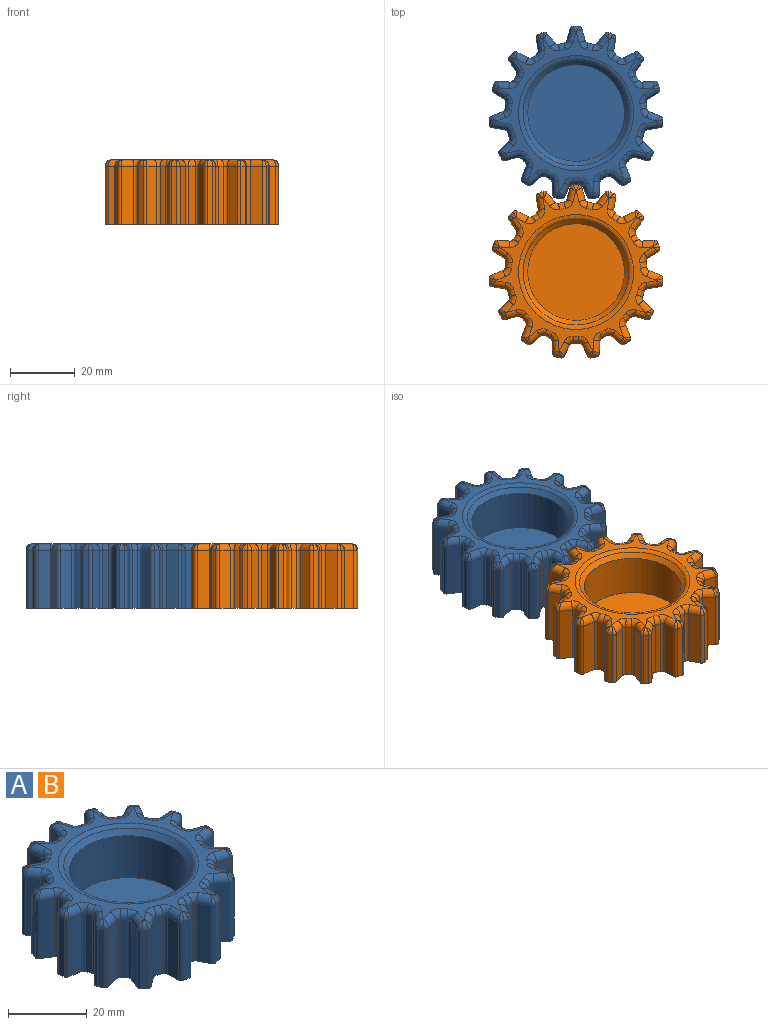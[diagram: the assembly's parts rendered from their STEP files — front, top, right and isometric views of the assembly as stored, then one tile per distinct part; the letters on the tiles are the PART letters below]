
ASSEMBLY  parts=2 mates=1
PART A: 246 faces, bbox 54x53.7x20 mm
  f0: cylinder r=1mm len=18mm, axis (0,0,-1), area 20.6mm2, adj f1,f119,f121,f242
  f1: cylinder r=22mm len=18mm, axis (0,0,-1), area 34.5mm2, adj f0,f2,f121,f240
  f2: cylinder r=1mm len=18mm, axis (0,0,-1), area 20.6mm2, adj f1,f3,f121,f238
  f3: plane 18x3.33mm, normal (0.84,-0.54,0), area 71.4mm2, adj f2,f4,f121,f236
  f4: cylinder r=1mm len=18mm, axis (0,0,-1), area 23.6mm2, adj f3,f5,f121,f234
  f5: plane 18x1.25mm, normal (0.74,0.67,0), area 30.2mm2, adj f4,f6,f121,f232
  f6: cylinder r=1mm len=18mm, axis (0,0,-1), area 23.6mm2, adj f5,f7,f121,f230
  f7: plane 18x3.54mm, normal (-0.45,0.89,0), area 71.4mm2, adj f6,f8,f121,f228
  f8: cylinder r=1mm len=18mm, axis (0,0,-1), area 20.6mm2, adj f7,f9,f121,f226
  f9: cylinder r=22mm len=18mm, axis (0,0,-1), area 34.5mm2, adj f8,f10,f121,f224
  f10: cylinder r=1mm len=18mm, axis (0,0,-1), area 20.6mm2, adj f9,f11,f121,f222
  f11: plane 18x3.92mm, normal (0.99,-0.16,0), area 71.4mm2, adj f10,f12,f121,f220
  f12: cylinder r=1mm len=18mm, axis (0,0,-1), area 23.6mm2, adj f11,f13,f121,f218
  f13: plane 18x1.53mm, normal (0.41,0.91,0), area 30.2mm2, adj f12,f14,f121,f216
  f14: cylinder r=1mm len=18mm, axis (0,0,-1), area 23.6mm2, adj f13,f15,f121,f214
  f15: plane 18x3.08mm, normal (-0.78,0.63,0), area 71.4mm2, adj f14,f16,f121,f212
  f16: cylinder r=1mm len=18mm, axis (0,0,-1), area 20.6mm2, adj f15,f17,f121,f210
  f17: cylinder r=22mm len=18mm, axis (0,0,-1), area 34.5mm2, adj f16,f18,f121,f208
  f18: cylinder r=1mm len=18mm, axis (0,0,-1), area 20.6mm2, adj f17,f19,f121,f206
  f19: plane 18x3.83mm, normal (0.97,0.26,0), area 71.4mm2, adj f18,f20,f121,f204
  f20: cylinder r=1mm len=18mm, axis (0,0,-1), area 23.6mm2, adj f19,f21,f121,f202
  f21: plane 18x1.68mm, normal (0,1,0), area 30.2mm2, adj f20,f22,f121,f200
  f22: cylinder r=1mm len=18mm, axis (0,0,-1), area 23.6mm2, adj f21,f23,f121,f198
  f23: plane 18x3.83mm, normal (-0.97,0.26,0), area 71.4mm2, adj f22,f24,f121,f196
  f24: cylinder r=1mm len=18mm, axis (0,0,-1), area 20.6mm2, adj f23,f25,f121,f194
  f25: cylinder r=22mm len=18mm, axis (0,0,-1), area 34.5mm2, adj f24,f26,f121,f192
  f26: cylinder r=1mm len=18mm, axis (0,0,-1), area 20.6mm2, adj f25,f27,f121,f190
  f27: plane 18x3.08mm, normal (0.78,0.63,0), area 71.4mm2, adj f26,f28,f121,f188
  f28: cylinder r=1mm len=18mm, axis (0,0,-1), area 23.6mm2, adj f27,f29,f121,f186
  f29: plane 18x1.53mm, normal (-0.41,0.91,0), area 30.2mm2, adj f28,f30,f121,f184
  f30: cylinder r=1mm len=18mm, axis (0,0,-1), area 23.6mm2, adj f29,f31,f121,f182
  f31: plane 18x3.92mm, normal (-0.99,-0.16,0), area 71.4mm2, adj f30,f32,f121,f180
  f32: cylinder r=1mm len=18mm, axis (0,0,-1), area 20.6mm2, adj f31,f33,f121,f178
  f33: cylinder r=22mm len=18mm, axis (0,0,-1), area 34.5mm2, adj f32,f34,f121,f176
  f34: cylinder r=1mm len=18mm, axis (0,0,-1), area 20.6mm2, adj f33,f35,f121,f174
  f35: plane 18x3.54mm, normal (0.45,0.89,0), area 71.4mm2, adj f34,f36,f121,f172
  f36: cylinder r=1mm len=18mm, axis (0,0,-1), area 23.6mm2, adj f35,f37,f121,f170
  f37: plane 18x1.25mm, normal (-0.74,0.67,0), area 30.2mm2, adj f36,f38,f121,f168
  f38: cylinder r=1mm len=18mm, axis (0,0,-1), area 23.6mm2, adj f37,f39,f121,f166
  f39: plane 18x3.33mm, normal (-0.84,-0.54,0), area 71.4mm2, adj f38,f40,f121,f164
  f40: cylinder r=1mm len=18mm, axis (0,0,-1), area 20.6mm2, adj f39,f41,f121,f162
  f41: cylinder r=22mm len=18mm, axis (0,0,-1), area 34.5mm2, adj f40,f42,f121,f160
  f42: cylinder r=1mm len=18mm, axis (0,0,-1), area 20.6mm2, adj f41,f43,f121,f158
  f43: plane 18x3.96mm, normal (0.05,1,0), area 71.4mm2, adj f42,f44,f121,f156
  f44: cylinder r=1mm len=18mm, axis (0,0,-1), area 23.6mm2, adj f43,f45,f121,f154
  f45: plane 18x1.59mm, normal (-0.95,0.31,0), area 30.2mm2, adj f44,f46,f121,f152
  f46: cylinder r=1mm len=18mm, axis (0,0,-1), area 23.6mm2, adj f45,f47,f121,f150
  f47: plane 18x3.33mm, normal (-0.54,-0.84,0), area 71.4mm2, adj f46,f48,f121,f148
  f48: cylinder r=1mm len=18mm, axis (0,0,-1), area 20.6mm2, adj f47,f49,f121,f146
  f49: cylinder r=22mm len=18mm, axis (0,0,-1), area 34.5mm2, adj f48,f50,f121,f144
  f50: cylinder r=1mm len=18mm, axis (0,0,-1), area 20.6mm2, adj f49,f51,f121,f142
  f51: plane 18x3.71mm, normal (-0.36,0.93,0), area 71.4mm2, adj f50,f52,f121,f140
  f52: cylinder r=1mm len=18mm, axis (0,0,-1), area 23.6mm2, adj f51,f53,f121,f138
  f53: plane 18x1.67mm, normal (-0.99,-0.1,0), area 30.2mm2, adj f52,f54,f121,f136
  f54: cylinder r=1mm len=18mm, axis (0,0,-1), area 23.6mm2, adj f53,f55,f121,f134
  f55: plane 18x3.92mm, normal (-0.16,-0.99,0), area 71.4mm2, adj f54,f56,f121,f132
  f56: cylinder r=1mm len=18mm, axis (0,0,-1), area 20.6mm2, adj f55,f57,f121,f130
  f57: cylinder r=22mm len=18mm, axis (0,0,-1), area 34.5mm2, adj f56,f58,f121,f128
  f58: cylinder r=1mm len=18mm, axis (0,0,-1), area 20.6mm2, adj f57,f59,f121,f126
  f59: plane 18x2.81mm, normal (-0.71,0.71,0), area 71.4mm2, adj f58,f60,f121,f127
  f60: cylinder r=1mm len=18mm, axis (0,0,-1), area 23.6mm2, adj f59,f61,f121,f129
  f61: plane 18x1.45mm, normal (-0.87,-0.5,0), area 30.2mm2, adj f60,f62,f121,f131
  f62: cylinder r=1mm len=18mm, axis (0,0,-1), area 23.6mm2, adj f61,f63,f121,f133
  f63: plane 18x3.83mm, normal (0.26,-0.97,0), area 71.4mm2, adj f62,f64,f121,f135
  f64: cylinder r=1mm len=18mm, axis (0,0,-1), area 20.6mm2, adj f63,f65,f121,f137
  f65: cylinder r=22mm len=18mm, axis (0,0,-1), area 34.5mm2, adj f64,f66,f121,f139
  f66: cylinder r=1mm len=18mm, axis (0,0,-1), area 20.6mm2, adj f65,f67,f121,f141
  f67: plane 18x3.71mm, normal (-0.93,0.36,0), area 71.4mm2, adj f66,f68,f121,f143
  f68: cylinder r=1mm len=18mm, axis (0,0,-1), area 23.6mm2, adj f67,f69,f121,f145
  f69: plane 18x1.36mm, normal (-0.59,-0.81,0), area 30.2mm2, adj f68,f70,f121,f147
  f70: cylinder r=1mm len=18mm, axis (0,0,-1), area 23.6mm2, adj f69,f71,f121,f149
  f71: plane 18x3.08mm, normal (0.63,-0.78,0), area 71.4mm2, adj f70,f72,f121,f151
  f72: cylinder r=1mm len=18mm, axis (0,0,-1), area 20.6mm2, adj f71,f73,f121,f153
  f73: cylinder r=22mm len=18mm, axis (0,0,-1), area 34.5mm2, adj f72,f74,f121,f155
  f74: cylinder r=1mm len=18mm, axis (0,0,-1), area 20.6mm2, adj f73,f75,f121,f157
  f75: plane 18x3.96mm, normal (-1,-0.05,0), area 71.4mm2, adj f74,f76,f121,f159
  f76: cylinder r=1mm len=18mm, axis (0,0,-1), area 23.6mm2, adj f75,f77,f121,f161
  f77: plane 18x1.64mm, normal (-0.21,-0.98,0), area 30.2mm2, adj f76,f78,f121,f163
  f78: cylinder r=1mm len=18mm, axis (0,0,-1), area 23.6mm2, adj f77,f79,f121,f165
  f79: plane 18x3.54mm, normal (0.89,-0.45,0), area 71.4mm2, adj f78,f80,f121,f167
  f80: cylinder r=1mm len=18mm, axis (0,0,-1), area 20.6mm2, adj f79,f81,f121,f169
  f81: cylinder r=22mm len=18mm, axis (0,0,-1), area 34.5mm2, adj f80,f82,f121,f171
  f82: cylinder r=1mm len=18mm, axis (0,0,-1), area 20.6mm2, adj f81,f83,f121,f173
  f83: plane 18x3.54mm, normal (-0.89,-0.45,0), area 71.4mm2, adj f82,f84,f121,f175
  f84: cylinder r=1mm len=18mm, axis (0,0,-1), area 23.6mm2, adj f83,f85,f121,f177
  f85: plane 18x1.64mm, normal (0.21,-0.98,0), area 30.2mm2, adj f84,f86,f121,f179
  f86: cylinder r=1mm len=18mm, axis (0,0,-1), area 23.6mm2, adj f85,f87,f121,f181
  f87: plane 18x3.96mm, normal (1,-0.05,0), area 71.4mm2, adj f86,f88,f121,f183
  f88: cylinder r=1mm len=18mm, axis (0,0,-1), area 20.6mm2, adj f87,f89,f121,f185
  f89: cylinder r=22mm len=18mm, axis (0,0,-1), area 34.5mm2, adj f88,f90,f121,f187
  f90: cylinder r=1mm len=18mm, axis (0,0,-1), area 20.6mm2, adj f89,f91,f121,f189
  f91: plane 18x3.08mm, normal (-0.63,-0.78,0), area 71.4mm2, adj f90,f92,f121,f191
  f92: cylinder r=1mm len=18mm, axis (0,0,-1), area 23.6mm2, adj f91,f93,f121,f193
  f93: plane 18x1.36mm, normal (0.59,-0.81,0), area 30.2mm2, adj f92,f94,f121,f195
  f94: cylinder r=1mm len=18mm, axis (0,0,-1), area 23.6mm2, adj f93,f95,f121,f197
  f95: plane 18x3.71mm, normal (0.93,0.36,0), area 71.4mm2, adj f94,f96,f121,f199
  f96: cylinder r=1mm len=18mm, axis (0,0,-1), area 20.6mm2, adj f95,f97,f121,f201
  f97: cylinder r=22mm len=18mm, axis (0,0,-1), area 34.5mm2, adj f96,f98,f121,f203
  f98: cylinder r=1mm len=18mm, axis (0,0,-1), area 20.6mm2, adj f97,f99,f121,f205
  f99: plane 18x3.83mm, normal (-0.26,-0.97,0), area 71.4mm2, adj f98,f100,f121,f207
  f100: cylinder r=1mm len=18mm, axis (0,0,-1), area 23.6mm2, adj f99,f101,f121,f209
  f101: plane 18x1.45mm, normal (0.87,-0.5,0), area 30.2mm2, adj f100,f102,f121,f211
  f102: cylinder r=1mm len=18mm, axis (0,0,-1), area 23.6mm2, adj f101,f103,f121,f213
  f103: plane 18x2.81mm, normal (0.71,0.71,0), area 71.4mm2, adj f102,f104,f121,f215
  f104: cylinder r=1mm len=18mm, axis (0,0,-1), area 20.6mm2, adj f103,f105,f121,f217
  f105: cylinder r=22mm len=18mm, axis (0,0,-1), area 34.5mm2, adj f104,f106,f121,f219
  f106: cylinder r=1mm len=18mm, axis (0,0,-1), area 20.6mm2, adj f105,f107,f121,f221
  f107: plane 18x3.92mm, normal (0.16,-0.99,0), area 71.4mm2, adj f106,f108,f121,f223
  f108: cylinder r=1mm len=18mm, axis (0,0,-1), area 23.6mm2, adj f107,f109,f121,f225
  f109: plane 18x1.67mm, normal (0.99,-0.1,0), area 30.2mm2, adj f108,f110,f121,f227
  f110: cylinder r=1mm len=18mm, axis (0,0,-1), area 23.6mm2, adj f109,f111,f121,f229
  f111: plane 18x3.71mm, normal (0.36,0.93,0), area 71.4mm2, adj f110,f112,f121,f231
  f112: cylinder r=1mm len=18mm, axis (0,0,-1), area 20.6mm2, adj f111,f113,f121,f233
  f113: cylinder r=22mm len=18mm, axis (0,0,-1), area 34.5mm2, adj f112,f114,f121,f235
  f114: cylinder r=1mm len=18mm, axis (0,0,-1), area 20.6mm2, adj f113,f115,f121,f237
  f115: plane 18x3.33mm, normal (0.54,-0.84,0), area 71.4mm2, adj f114,f116,f121,f239
  f116: cylinder r=1mm len=18mm, axis (0,0,-1), area 23.6mm2, adj f115,f117,f121,f241
  f117: plane 18x1.59mm, normal (0.95,0.31,0), area 30.2mm2, adj f116,f118,f121,f243
  f118: cylinder r=1mm len=18mm, axis (0,0,-1), area 23.6mm2, adj f117,f119,f121,f245
  f119: plane 18x3.96mm, normal (-0.05,1,0), area 71.4mm2, adj f0,f118,f121,f244
  f120: plane 49.74x49.47mm, normal (0,0,1), area 390.9mm2, adj f125,f126,f127,f128,f130,f131,f132,f135
  f121: plane 53.89x53.61mm, normal (0,0,-1), area 1866.6mm2, adj f0,f1,f2,f3,f4,f5,f6,f7
  f122: cylinder r=15mm len=30mm, axis (0,0,1), area 1225.2mm2, adj f123,f124
  f123: plane 30x30mm, normal (0,0,1), area 706.9mm2, adj f122
  f124: cone r=15mm half-angle=45deg, axis (0,0,1), area 197.4mm2, adj f122,f125
  f125: torus R=17.83mm, axis (0,0,1), area 168.6mm2, adj f120,f124
  f126: torus R=3mm, axis (0,0,1), area 6.2mm2, adj f58,f120,f127,f128
  f127: cylinder r=2mm len=4.22mm, axis (0.71,0.71,0), area 11.6mm2, adj f59,f120,f126,f129
  f128: torus R=20mm, axis (0,0,1), area 5.8mm2, adj f57,f120,f126,f130
  f129: bspline ~2.5x2.34mm, area 2.7mm2, adj f60,f127,f131
  f130: torus R=3mm, axis (0,0,1), area 6.2mm2, adj f56,f120,f128,f132
  f131: cylinder r=2mm len=2.57mm, axis (-0.5,0.87,0), area 3.5mm2, adj f61,f120,f129,f133
  f132: cylinder r=2mm len=4.23mm, axis (-0.99,0.16,0), area 11.6mm2, adj f55,f120,f130,f134
  f133: bspline ~2.34x2.33mm, area 2.7mm2, adj f62,f131,f135
  f134: bspline ~2.34x1.91mm, area 2.7mm2, adj f54,f132,f136
  f135: cylinder r=2mm len=4.35mm, axis (-0.97,-0.26,0), area 11.6mm2, adj f63,f120,f133,f137
  f136: cylinder r=2mm len=2.16mm, axis (-0.1,0.99,0), area 3.5mm2, adj f53,f120,f134,f138
  f137: torus R=3mm, axis (0,0,1), area 6.2mm2, adj f64,f120,f135,f139
  f138: bspline ~2.34x2.15mm, area 2.7mm2, adj f52,f136,f140
  f139: torus R=20mm, axis (0,0,1), area 5.8mm2, adj f65,f120,f137,f141
  f140: cylinder r=2mm len=4.42mm, axis (0.93,0.36,0), area 11.6mm2, adj f51,f120,f138,f142
  f141: torus R=3mm, axis (0,0,1), area 6.2mm2, adj f66,f120,f139,f143
  f142: torus R=3mm, axis (0,0,1), area 6.2mm2, adj f50,f120,f140,f144
  f143: cylinder r=2mm len=4.42mm, axis (0.36,0.93,0), area 11.6mm2, adj f67,f120,f141,f145
  f144: torus R=20mm, axis (0,0,1), area 5.8mm2, adj f49,f120,f142,f146
  f145: bspline ~2.42x2.34mm, area 2.7mm2, adj f68,f143,f147
  f146: torus R=3mm, axis (0,0,1), area 6.2mm2, adj f48,f120,f144,f148
  f147: cylinder r=2mm len=2.6mm, axis (-0.81,0.59,0), area 3.5mm2, adj f69,f120,f145,f149
  f148: cylinder r=2mm len=4.42mm, axis (-0.84,0.54,0), area 11.6mm2, adj f47,f120,f146,f150
  f149: bspline ~2.52x2.34mm, area 2.7mm2, adj f70,f147,f151
  f150: bspline ~2.38x2.34mm, area 2.7mm2, adj f46,f148,f152
  f151: cylinder r=2mm len=4.34mm, axis (-0.78,-0.63,0), area 11.6mm2, adj f71,f120,f149,f153
  f152: cylinder r=2mm len=2.42mm, axis (0.31,0.95,0), area 3.5mm2, adj f45,f120,f150,f154
  f153: torus R=3mm, axis (0,0,1), area 6.2mm2, adj f72,f120,f151,f155
  f154: bspline ~2.34x2.08mm, area 2.7mm2, adj f44,f152,f156
  f155: torus R=20mm, axis (0,0,1), area 5.8mm2, adj f73,f120,f153,f157
  f156: cylinder r=2mm len=4.07mm, axis (1,-0.05,0), area 11.6mm2, adj f43,f120,f154,f158
  f157: torus R=3mm, axis (0,0,1), area 6.2mm2, adj f74,f120,f155,f159
  f158: torus R=3mm, axis (0,0,1), area 6.2mm2, adj f42,f120,f156,f160
  f159: cylinder r=2mm len=4.07mm, axis (-0.05,1,0), area 11.6mm2, adj f75,f120,f157,f161
  f160: torus R=20mm, axis (0,0,1), area 5.8mm2, adj f41,f120,f158,f162
  f161: bspline ~2.34x1.96mm, area 2.7mm2, adj f76,f159,f163
  f162: torus R=3mm, axis (0,0,1), area 6.2mm2, adj f40,f120,f160,f164
  f163: cylinder r=2mm len=2.3mm, axis (-0.98,0.21,0), area 3.5mm2, adj f77,f120,f161,f165
  f164: cylinder r=2mm len=4.42mm, axis (-0.54,0.84,0), area 11.6mm2, adj f39,f120,f162,f166
  f165: bspline ~2.34x2.28mm, area 2.7mm2, adj f78,f163,f167
  f166: bspline ~2.51x2.34mm, area 2.7mm2, adj f38,f164,f168
  f167: cylinder r=2mm len=4.44mm, axis (-0.45,-0.89,0), area 11.6mm2, adj f79,f120,f165,f169
  f168: cylinder r=2mm len=2.61mm, axis (0.67,0.74,0), area 3.5mm2, adj f37,f120,f166,f170
  f169: torus R=3mm, axis (0,0,1), area 6.2mm2, adj f80,f120,f167,f171
  f170: bspline ~2.48x2.34mm, area 2.7mm2, adj f36,f168,f172
  f171: torus R=20mm, axis (0,0,1), area 5.8mm2, adj f81,f120,f169,f173
  f172: cylinder r=2mm len=4.44mm, axis (0.89,-0.45,0), area 11.6mm2, adj f35,f120,f170,f174
  f173: torus R=3mm, axis (0,0,1), area 6.2mm2, adj f82,f120,f171,f175
  f174: torus R=3mm, axis (0,0,1), area 6.2mm2, adj f34,f120,f172,f176
  f175: cylinder r=2mm len=4.44mm, axis (-0.45,0.89,0), area 11.6mm2, adj f83,f120,f173,f177
  f176: torus R=20mm, axis (0,0,1), area 5.8mm2, adj f33,f120,f174,f178
  f177: bspline ~2.34x2.28mm, area 2.7mm2, adj f84,f175,f179
  f178: torus R=3mm, axis (0,0,1), area 6.2mm2, adj f32,f120,f176,f180
  f179: cylinder r=2mm len=2.3mm, axis (-0.98,-0.21,0), area 3.5mm2, adj f85,f120,f177,f181
  f180: cylinder r=2mm len=4.23mm, axis (-0.16,0.99,0), area 11.6mm2, adj f31,f120,f178,f182
  f181: bspline ~2.34x1.96mm, area 2.7mm2, adj f86,f179,f183
  f182: bspline ~2.34x2.22mm, area 2.7mm2, adj f30,f180,f184
  f183: cylinder r=2mm len=4.07mm, axis (-0.05,-1,0), area 11.6mm2, adj f87,f120,f181,f185
  f184: cylinder r=2mm len=2.51mm, axis (0.91,0.41,0), area 3.5mm2, adj f29,f120,f182,f186
  f185: torus R=3mm, axis (0,0,1), area 6.2mm2, adj f88,f120,f183,f187
  f186: bspline ~2.45x2.34mm, area 2.7mm2, adj f28,f184,f188
  f187: torus R=20mm, axis (0,0,1), area 5.8mm2, adj f89,f120,f185,f189
  f188: cylinder r=2mm len=4.34mm, axis (0.63,-0.78,0), area 11.6mm2, adj f27,f120,f186,f190
  f189: torus R=3mm, axis (0,0,1), area 6.2mm2, adj f90,f120,f187,f191
  f190: torus R=3mm, axis (0,0,1), area 6.2mm2, adj f26,f120,f188,f192
  f191: cylinder r=2mm len=4.34mm, axis (-0.78,0.63,0), area 11.6mm2, adj f91,f120,f189,f193
  f192: torus R=20mm, axis (0,0,1), area 5.8mm2, adj f25,f120,f190,f194
  f193: bspline ~2.52x2.34mm, area 2.7mm2, adj f92,f191,f195
  f194: torus R=3mm, axis (0,0,1), area 6.2mm2, adj f24,f120,f192,f196
  f195: cylinder r=2mm len=2.6mm, axis (-0.81,-0.59,0), area 3.5mm2, adj f93,f120,f193,f197
  f196: cylinder r=2mm len=4.35mm, axis (0.26,0.97,0), area 11.6mm2, adj f23,f120,f194,f198
  f197: bspline ~2.42x2.34mm, area 2.7mm2, adj f94,f195,f199
  f198: bspline ~2.34x2mm, area 2.7mm2, adj f22,f196,f200
  f199: cylinder r=2mm len=4.42mm, axis (0.36,-0.93,0), area 11.6mm2, adj f95,f120,f197,f201
  f200: cylinder r=2mm len=2mm, axis (1,0,0), area 3.5mm2, adj f21,f120,f198,f202
  f201: torus R=3mm, axis (0,0,1), area 6.2mm2, adj f96,f120,f199,f203
  f202: bspline ~2.34x2mm, area 2.7mm2, adj f20,f200,f204
  f203: torus R=20mm, axis (0,0,1), area 5.8mm2, adj f97,f120,f201,f205
  f204: cylinder r=2mm len=4.35mm, axis (0.26,-0.97,0), area 11.6mm2, adj f19,f120,f202,f206
  f205: torus R=3mm, axis (0,0,1), area 6.2mm2, adj f98,f120,f203,f207
  f206: torus R=3mm, axis (0,0,1), area 6.2mm2, adj f18,f120,f204,f208
  f207: cylinder r=2mm len=4.35mm, axis (-0.97,0.26,0), area 11.6mm2, adj f99,f120,f205,f209
  f208: torus R=20mm, axis (0,0,1), area 5.8mm2, adj f17,f120,f206,f210
  f209: bspline ~2.34x2.33mm, area 2.7mm2, adj f100,f207,f211
  f210: torus R=3mm, axis (0,0,1), area 6.2mm2, adj f16,f120,f208,f212
  f211: cylinder r=2mm len=2.57mm, axis (-0.5,-0.87,0), area 3.5mm2, adj f101,f120,f209,f213
  f212: cylinder r=2mm len=4.34mm, axis (0.63,0.78,0), area 11.6mm2, adj f15,f120,f210,f214
  f213: bspline ~2.5x2.34mm, area 2.7mm2, adj f102,f211,f215
  f214: bspline ~2.45x2.34mm, area 2.7mm2, adj f14,f212,f216
  f215: cylinder r=2mm len=4.22mm, axis (0.71,-0.71,0), area 11.6mm2, adj f103,f120,f213,f217
  f216: cylinder r=2mm len=2.51mm, axis (0.91,-0.41,0), area 3.5mm2, adj f13,f120,f214,f218
  f217: torus R=3mm, axis (0,0,1), area 6.2mm2, adj f104,f120,f215,f219
  f218: bspline ~2.34x2.22mm, area 2.7mm2, adj f12,f216,f220
  f219: torus R=20mm, axis (0,0,1), area 5.8mm2, adj f105,f120,f217,f221
  f220: cylinder r=2mm len=4.23mm, axis (-0.16,-0.99,0), area 11.6mm2, adj f11,f120,f218,f222
  f221: torus R=3mm, axis (0,0,1), area 6.2mm2, adj f106,f120,f219,f223
  f222: torus R=3mm, axis (0,0,1), area 6.2mm2, adj f10,f120,f220,f224
  f223: cylinder r=2mm len=4.23mm, axis (-0.99,-0.16,0), area 11.6mm2, adj f107,f120,f221,f225
  f224: torus R=20mm, axis (0,0,1), area 5.8mm2, adj f9,f120,f222,f226
  f225: bspline ~2.34x1.91mm, area 2.7mm2, adj f108,f223,f227
  f226: torus R=3mm, axis (0,0,1), area 6.2mm2, adj f8,f120,f224,f228
  f227: cylinder r=2mm len=2.16mm, axis (-0.1,-0.99,0), area 3.5mm2, adj f109,f120,f225,f229
  f228: cylinder r=2mm len=4.44mm, axis (0.89,0.45,0), area 11.6mm2, adj f7,f120,f226,f230
  f229: bspline ~2.34x2.15mm, area 2.7mm2, adj f110,f227,f231
  f230: bspline ~2.48x2.34mm, area 2.7mm2, adj f6,f228,f232
  f231: cylinder r=2mm len=4.42mm, axis (0.93,-0.36,0), area 11.6mm2, adj f111,f120,f229,f233
  f232: cylinder r=2mm len=2.61mm, axis (0.67,-0.74,0), area 3.5mm2, adj f5,f120,f230,f234
  f233: torus R=3mm, axis (0,0,1), area 6.2mm2, adj f112,f120,f231,f235
  f234: bspline ~2.51x2.34mm, area 2.7mm2, adj f4,f232,f236
  f235: torus R=20mm, axis (0,0,1), area 5.8mm2, adj f113,f120,f233,f237
  f236: cylinder r=2mm len=4.42mm, axis (-0.54,-0.84,0), area 11.6mm2, adj f3,f120,f234,f238
  f237: torus R=3mm, axis (0,0,1), area 6.2mm2, adj f114,f120,f235,f239
  f238: torus R=3mm, axis (0,0,1), area 6.2mm2, adj f2,f120,f236,f240
  f239: cylinder r=2mm len=4.42mm, axis (-0.84,-0.54,0), area 11.6mm2, adj f115,f120,f237,f241
  f240: torus R=20mm, axis (0,0,1), area 5.8mm2, adj f1,f120,f238,f242
  f241: bspline ~2.38x2.34mm, area 2.7mm2, adj f116,f239,f243
  f242: torus R=3mm, axis (0,0,1), area 6.2mm2, adj f0,f120,f240,f244
  f243: cylinder r=2mm len=2.42mm, axis (0.31,-0.95,0), area 3.5mm2, adj f117,f120,f241,f245
  f244: cylinder r=2mm len=4.07mm, axis (1,0.05,0), area 11.6mm2, adj f119,f120,f242,f245
  f245: bspline ~2.34x2.08mm, area 2.7mm2, adj f118,f243,f244
PART B: same geometry as A
PLACE A t=(-0.17,1.42,-7.43)mm
PLACE B t=(-0.17,-47.88,-7.43)mm
MATE planar A.f1 <-> B.f1  axis (0,0,-1) through (-0.17,1.42,-7.43)mm
